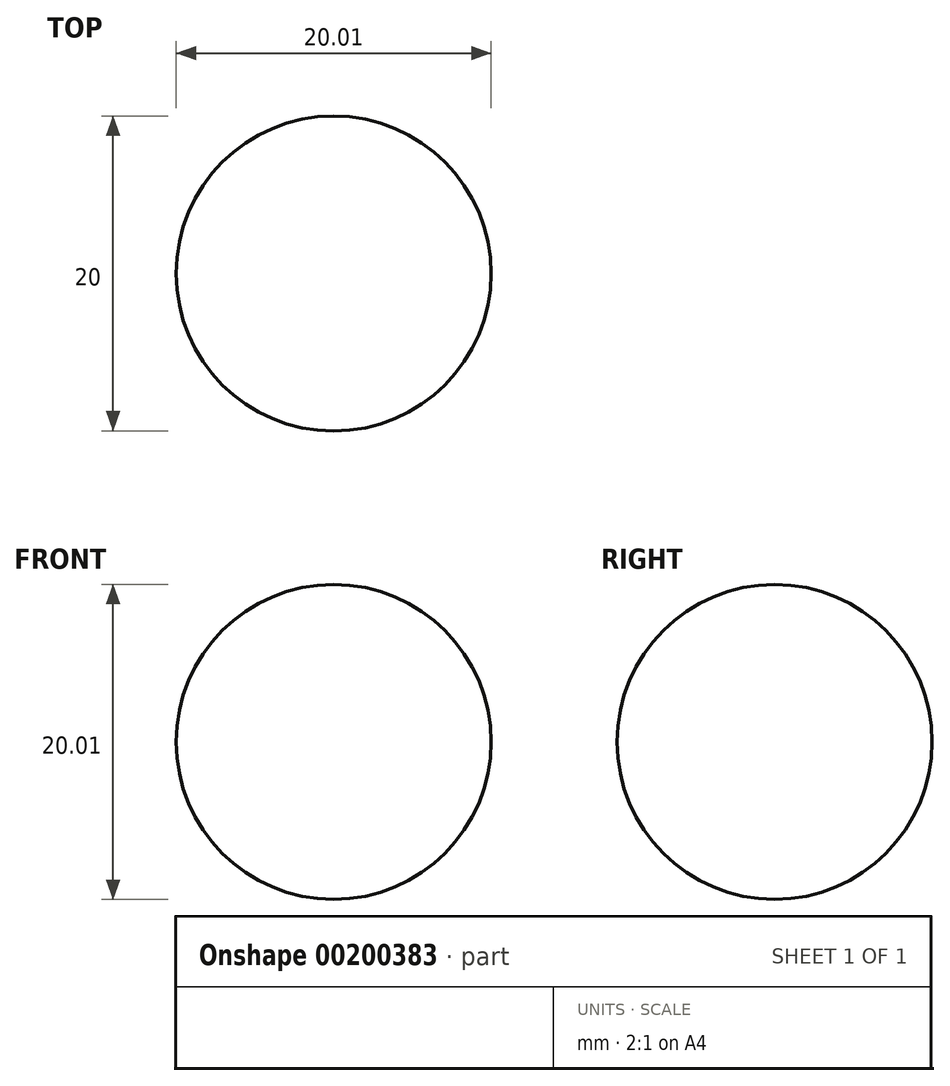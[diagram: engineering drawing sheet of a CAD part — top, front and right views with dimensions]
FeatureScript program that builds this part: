
annotation { "Feature Type Name" : "Feature", "Feature Type Description" : "" }
export const myFeature = defineFeature(function(context is Context, id is Id, definition is map)
    precondition{}
    {
        {
            var Q0;
            Q0=qCreatedBy(makeId("Front.planeOp"),FACE);
            var sketch = newSketch(context, id + "F0", { "sketchPlane" : qUnion([Q0])});
            skCircle(sketch, "E0", {"center": v(-41.43, 32.63) * mm, "radius": 10 * mm});
            skLineSegment(sketch, "E1", {"start": v(-41.43, 42.63) * mm, "end": v(-41.43, 22.62) * mm});
            skSolve(sketch);
        }
        {
            var Q0;
            {var subQ0=sQuery(id+"F0.wireOp",EDGE,"E1");Q0=makeQuery(id+"F0.imprint","IMPRINT",FACE,{"disambiguationData":[TD([[makeQuery(id+"F0.imprint","IMPRINT",EDGE,{"derivedFrom":subQ0}),-1.0]])]});}
            var Q1;
            Q1=sQuery(id+"F0.wireOp",EDGE,"E1");
            revolve(context, id + "F1", {"entities" : qUnion([Q0]), "axis" : qUnion([Q1]), "revolveType" : RevolveType.FULL});
        }
    });
